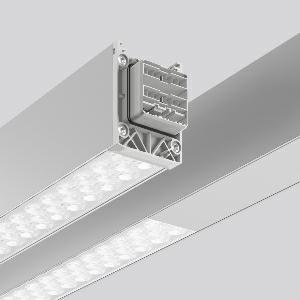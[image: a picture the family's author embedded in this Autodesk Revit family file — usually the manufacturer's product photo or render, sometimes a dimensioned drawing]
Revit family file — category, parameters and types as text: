
# Revit family: linedo_4_5m_90_10001000_954590_850_476_701_908e
name_source: partatom
category: Lighting Fixtures
units: mm (PartAtom-declared; Revit-internal decimal feet)

## family parameters
Cut with Voids When Loaded = No
Host = Face
Light Source = No
Part Type = Normal
Room Calculation Point = No
Round Connector Dimension = Use Diameter
Shared = No

## types (1)
- LINEDO_4,5m_90_10001000 (1 x LED Modul 850, 2475 lm, 5000)
    Apparent Load = 31 VA
    CIE Flux Codes = 73 96 99 100 100
    Color Rendering = 80
    Color Temperature = 5000
    Default Elevation = 1800 mm
    Description = LINEDO, 31 W, 4950 lm, 850, aluminium, DALI
Continuous line luminaire, L 4547 B 58 H 76
    Height = 76 mm
    Lamp = 1 x LED Modul 850
    Lamp Light Flux = 2475 lm
    Lamp count = 1
    Length = 4547 mm
    Lifetime = 50000 h
    Luminous efficacy = 160 lm/W
    Manufacturer = RZB
    ModVariant = No
    Model = 954590.850.476.701
    Mounting Place = Ceiling
    Mounting Type = Surface mounted, Pendant
    Number of Poles = 1
    OnlyDefault = Yes
    Power Factor = 1
    Product Name = LINEDO_4,5m_90_10001000
    Product group = Surface mounted continuous line luminaire system
    ProductGroupID = 310
    Protection Class = Protection class I
    Protection Degree = IP 54
    RLX_Detail_Level = 1
    RLX_Emergency_Light_Flux = 0 lm
    RLX_Emergency_Type = 0
    RLX_Emergency_Type_DB = No
    RlxData = <blob elided: 52405 chars, md5=e5b8b339>
    Socket = socket
    Standby Power = 0 W
    System Light Flux = 4950 lm
    System Power = 31 W
    Type Comments = Product without accessories
    Type Image = 954590.850.476.504.jpg
    URL = http://relux.com
    VarID = ---
    Voltage = 230 V
    Voltage Range = 220-240 V
    Weight = 0.00 kg
    Width = 58 mm

## geometry (parser evidence)
native form markers: Blend x4, Sweep x15
no freeform markers — native parametric forms only
